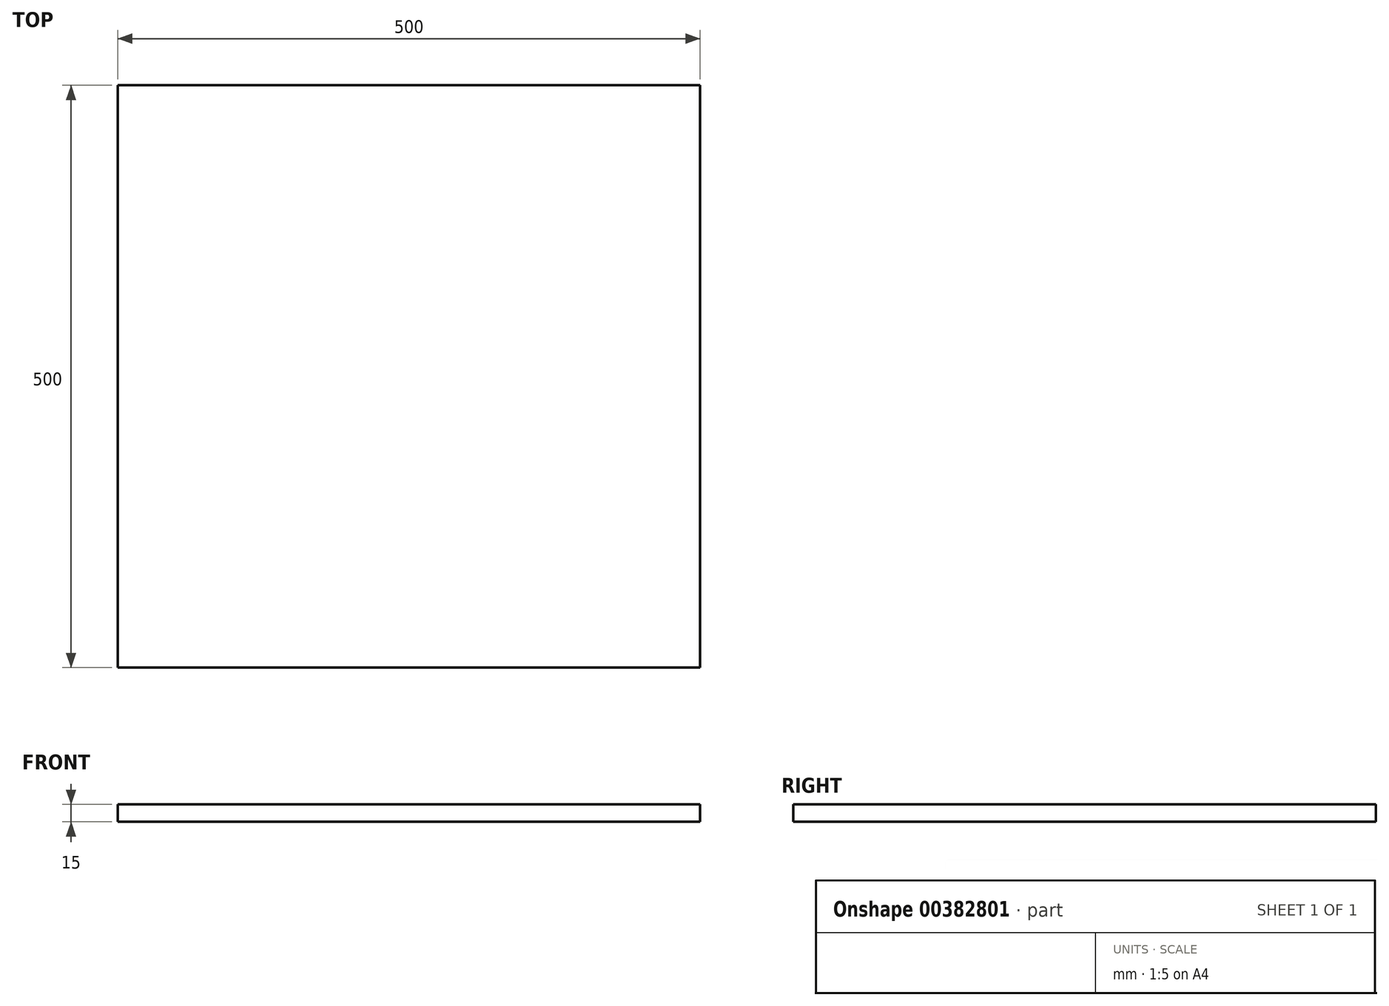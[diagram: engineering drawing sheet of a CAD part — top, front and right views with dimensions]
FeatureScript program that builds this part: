
annotation { "Feature Type Name" : "Feature", "Feature Type Description" : "" }
export const myFeature = defineFeature(function(context is Context, id is Id, definition is map)
    precondition{}
    {
        {
            var Q0;
            Q0=qCreatedBy(makeId("Top.planeOp"),FACE);
            var sketch = newSketch(context, id + "F0", { "sketchPlane" : qUnion([Q0])});
            skLineSegment(sketch, "E0.bottom", {"start": v(250, 250) * mm, "end": v(-250, 250) * mm});
            skLineSegment(sketch, "E0.top", {"start": v(250, -250) * mm, "end": v(-250, -250) * mm});
            skLineSegment(sketch, "E0.left", {"start": v(250, 250) * mm, "end": v(250, -250) * mm});
            skLineSegment(sketch, "E0.right", {"start": v(-250, 250) * mm, "end": v(-250, -250) * mm});
            skPoint(sketch, "E0.middle", {"position": v(0, 0) * mm});
            skSolve(sketch);
        }
        {
            var Q0;
            Q0=makeQuery(id+"F0.imprint","IMPRINT",FACE,{"disambiguationData":[TD([[makeQuery(id+"F0.imprint","IMPRINT",EDGE,{"derivedFrom":sQuery(id+"F0.wireOp",EDGE,"E0.bottom")}),1.0]])]});
            extrude(context, id + "F1", {"entities" : qUnion([Q0]), "depth" : 15 * mm, "offsetDistance" : 25 * mm});
        }
    });
